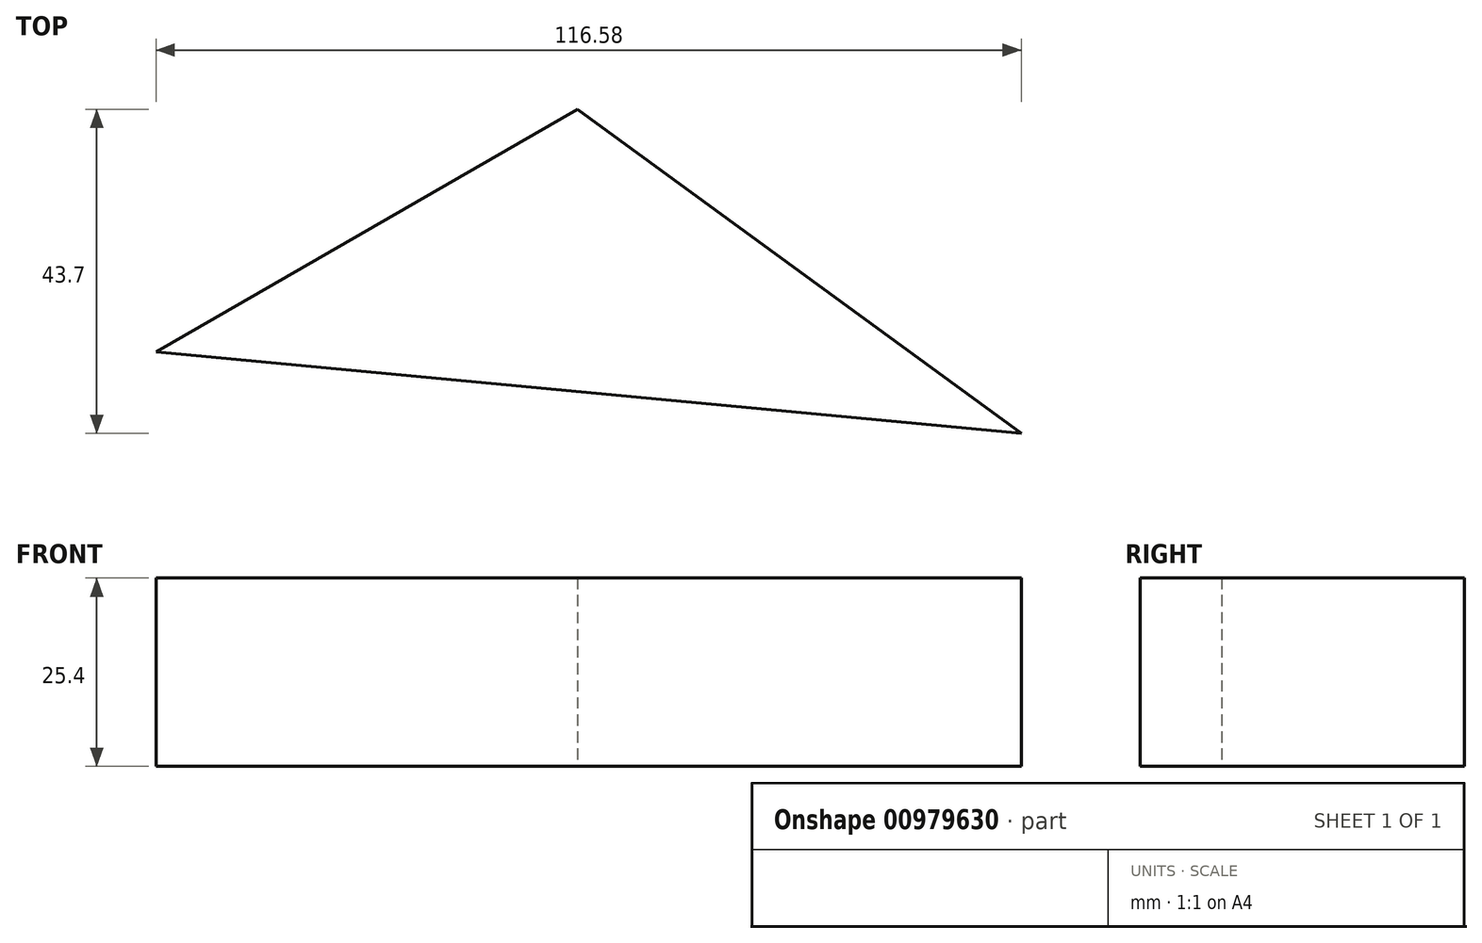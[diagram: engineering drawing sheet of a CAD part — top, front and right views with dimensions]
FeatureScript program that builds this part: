
annotation { "Feature Type Name" : "Feature", "Feature Type Description" : "" }
export const myFeature = defineFeature(function(context is Context, id is Id, definition is map)
    precondition{}
    {
        {
            var Q0;
            Q0=qCreatedBy(makeId("Top.planeOp"),FACE);
            var sketch = newSketch(context, id + "F0", { "sketchPlane" : qUnion([Q0])});
            skLineSegment(sketch, "E0", {"start": v(-58.72, -19.62) * mm, "end": v(-1.97, 13.1) * mm});
            skLineSegment(sketch, "E1", {"start": v(-1.97, 13.1) * mm, "end": v(57.86, -30.59) * mm});
            skLineSegment(sketch, "E2", {"start": v(-58.72, -19.62) * mm, "end": v(57.86, -30.59) * mm});
            skSolve(sketch);
        }
        {
            var Q0;
            Q0=makeQuery(id+"F0.imprint","IMPRINT",FACE,{"disambiguationData":[TD([[makeQuery(id+"F0.imprint","IMPRINT",EDGE,{"derivedFrom":sQuery(id+"F0.wireOp",EDGE,"E0")}),-1.0]])]});
            extrude(context, id + "F1", {"entities" : qUnion([Q0]), "depth" : 25.4 * mm, "offsetDistance" : 25.4 * mm});
        }
    });
